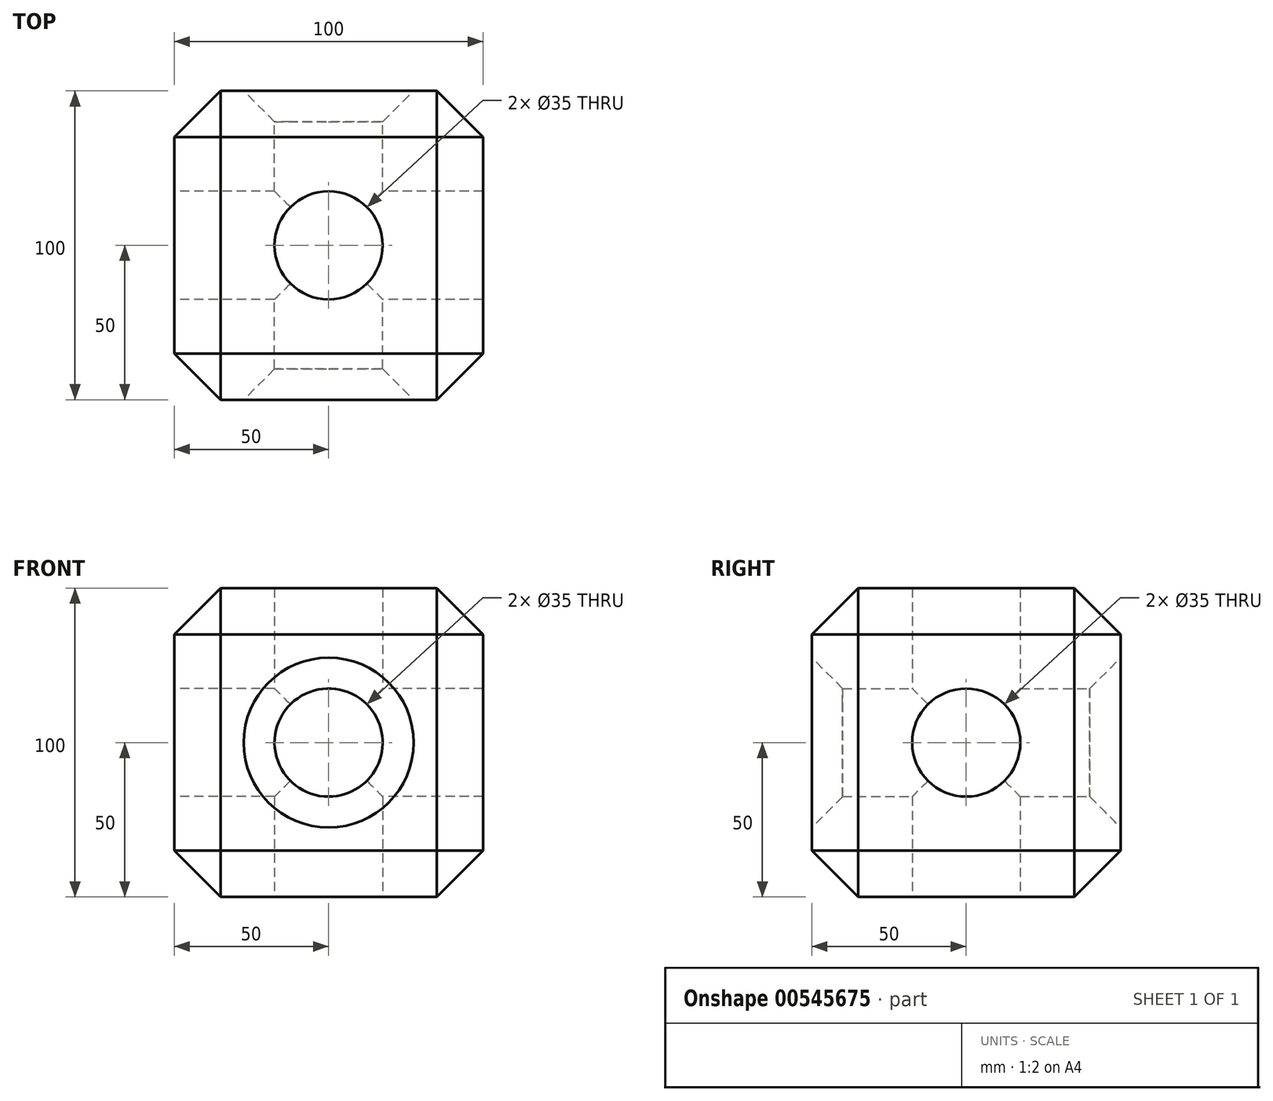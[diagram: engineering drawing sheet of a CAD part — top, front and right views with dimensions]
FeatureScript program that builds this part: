
annotation { "Feature Type Name" : "Feature", "Feature Type Description" : "" }
export const myFeature = defineFeature(function(context is Context, id is Id, definition is map)
    precondition{}
    {
        {
            var Q0;
            Q0=qCreatedBy(makeId("Front.planeOp"),FACE);
            var sketch = newSketch(context, id + "F0", { "sketchPlane" : qUnion([Q0])});
            skLineSegment(sketch, "E0.bottom", {"start": v(50, -50) * mm, "end": v(-50, -50) * mm});
            skLineSegment(sketch, "E0.top", {"start": v(50, 50) * mm, "end": v(-50, 50) * mm});
            skLineSegment(sketch, "E0.left", {"start": v(50, -50) * mm, "end": v(50, 50) * mm});
            skLineSegment(sketch, "E0.right", {"start": v(-50, -50) * mm, "end": v(-50, 50) * mm});
            skPoint(sketch, "E0.middle", {"position": v(0, 0) * mm});
            skCircle(sketch, "E1", {"center": v(0, 0) * mm, "radius": 17.5 * mm});
            skSolve(sketch);
        }
        {
            var Q0;
            Q0=makeQuery(id+"F0.imprint","IMPRINT",FACE,{"disambiguationData":[TD([[makeQuery(id+"F0.imprint","IMPRINT",EDGE,{"derivedFrom":sQuery(id+"F0.wireOp",EDGE,"E0.bottom")}),-1.0]])]});
            extrude(context, id + "F1", {"entities" : qUnion([Q0]), "endBound" : BoundingType.SYMMETRIC, "depth" : 100 * mm, "offsetDistance" : 25 * mm});
        }
        {
            var Q0;
            Q0=makeQuery(id+"F1.opExtrude","SWEPT_FACE",FACE,{"disambiguationData":[OSD([sQuery(id+"F0.wireOp",EDGE,"E0.right")])]});
            var sketch = newSketch(context, id + "F2", { "sketchPlane" : qUnion([Q0])});
            skCircle(sketch, "E2", {"center": v(0, 0) * mm, "radius": 17.5 * mm});
            skSolve(sketch);
        }
        {
            var Q0;
            Q0=makeQuery(id+"F2.imprint","IMPRINT",FACE,{"disambiguationData":[TD([[makeQuery(id+"F2.imprint","IMPRINT",EDGE,{"derivedFrom":sQuery(id+"F2.wireOp",EDGE,"E2")}),1.0]])]});
            var Q1;
            Q1=makeQuery(id+"F1.opExtrude","SWEPT_FACE",FACE,{"disambiguationData":[OSD([sQuery(id+"F0.wireOp",EDGE,"E0.left")])]});
            extrude(context, id + "F3", {"entities" : qUnion([Q0]), "operationType" : NewBodyOperationType.REMOVE, "endBound" : BoundingType.UP_TO_SURFACE, "oppositeDirection" : true, "depth" : 25 * mm, "endBoundEntityFace" : qUnion([Q1]), "offsetDistance" : 25 * mm});
        }
        {
            var Q0;
            Q0=makeQuery(id+"F1.opExtrude","SWEPT_FACE",FACE,{"disambiguationData":[OSD([sQuery(id+"F0.wireOp",EDGE,"E0.bottom")])]});
            var sketch = newSketch(context, id + "F4", { "sketchPlane" : qUnion([Q0])});
            skCircle(sketch, "E3", {"center": v(0, 0) * mm, "radius": 17.5 * mm});
            skSolve(sketch);
        }
        {
            var Q0;
            Q0=makeQuery(id+"F4.imprint","IMPRINT",FACE,{"disambiguationData":[TD([[makeQuery(id+"F4.imprint","IMPRINT",EDGE,{"derivedFrom":sQuery(id+"F4.wireOp",EDGE,"E3")}),1.0]])]});
            var Q1;
            Q1=makeQuery(id+"F1.opExtrude","SWEPT_FACE",FACE,{"disambiguationData":[OSD([sQuery(id+"F0.wireOp",EDGE,"E0.top")])]});
            extrude(context, id + "F5", {"entities" : qUnion([Q0]), "operationType" : NewBodyOperationType.REMOVE, "endBound" : BoundingType.UP_TO_SURFACE, "oppositeDirection" : true, "depth" : 25 * mm, "endBoundEntityFace" : qUnion([Q1]), "offsetDistance" : 25 * mm});
        }
        {
            var Q0;
            Q0=makeQuery(id+"F1.opExtrude","CAP_EDGE",EDGE,{"disambiguationData":[OSD([sQuery(id+"F0.wireOp",EDGE,"E0.top")])],"isStart":true});
            var Q1;
            Q1=makeQuery(id+"F1.opExtrude","SWEPT_EDGE",EDGE,{"disambiguationData":[OSD([sQuery(id+"F0.wireOp",EDGE,"E0.top"),sQuery(id+"F0.wireOp",EDGE,"E0.left")])]});
            var Q2;
            Q2=makeQuery(id+"F1.opExtrude","CAP_EDGE",EDGE,{"disambiguationData":[OSD([sQuery(id+"F0.wireOp",EDGE,"E0.top")])],"isStart":false});
            var Q3;
            Q3=makeQuery(id+"F1.opExtrude","SWEPT_EDGE",EDGE,{"disambiguationData":[OSD([sQuery(id+"F0.wireOp",EDGE,"E0.top"),sQuery(id+"F0.wireOp",EDGE,"E0.right")])]});
            var Q4;
            Q4=makeQuery(id+"F1.opExtrude","CAP_EDGE",EDGE,{"disambiguationData":[OSD([sQuery(id+"F0.wireOp",EDGE,"E0.right")])],"isStart":true});
            var Q5;
            Q5=makeQuery(id+"F1.opExtrude","CAP_EDGE",EDGE,{"disambiguationData":[OSD([sQuery(id+"F0.wireOp",EDGE,"E0.right")])],"isStart":false});
            var Q6;
            Q6=makeQuery(id+"F1.opExtrude","SWEPT_EDGE",EDGE,{"disambiguationData":[OSD([sQuery(id+"F0.wireOp",EDGE,"E0.bottom"),sQuery(id+"F0.wireOp",EDGE,"E0.right")])]});
            var Q7;
            Q7=makeQuery(id+"F1.opExtrude","CAP_EDGE",EDGE,{"disambiguationData":[OSD([sQuery(id+"F0.wireOp",EDGE,"E0.bottom")])],"isStart":true});
            var Q8;
            Q8=makeQuery(id+"F1.opExtrude","SWEPT_EDGE",EDGE,{"disambiguationData":[OSD([sQuery(id+"F0.wireOp",EDGE,"E0.bottom"),sQuery(id+"F0.wireOp",EDGE,"E0.left")])]});
            var Q9;
            Q9=makeQuery(id+"F1.opExtrude","CAP_EDGE",EDGE,{"disambiguationData":[OSD([sQuery(id+"F0.wireOp",EDGE,"E0.left")])],"isStart":false});
            var Q10;
            Q10=makeQuery(id+"F1.opExtrude","CAP_EDGE",EDGE,{"disambiguationData":[OSD([sQuery(id+"F0.wireOp",EDGE,"E0.bottom")])],"isStart":false});
            var Q11;
            Q11=makeQuery(id+"F1.opExtrude","CAP_EDGE",EDGE,{"disambiguationData":[OSD([sQuery(id+"F0.wireOp",EDGE,"E0.left")])],"isStart":true});
            chamfer(context, id + "F6", {"entities" : qUnion([Q0, Q1, Q2, Q3, Q4, Q5, Q6, Q7, Q8, Q9, Q10, Q11]), "width" : 15 * mm, "tangentPropagation" : true});
        }
        {
            var Q0;
            Q0=makeQuery(id+"F3.boolean.opBoolean","COPY",EDGE,{"derivedFrom":makeQuery(id+"F3.opExtrude","TWEAK_EDGE",EDGE,{"derivedFrom":[makeQuery(id+"F1.opExtrude","SWEPT_FACE",FACE,{"disambiguationData":[OSD([sQuery(id+"F0.wireOp",EDGE,"E0.left")])]}),makeQuery(id+"F2.imprint","IMPRINT",EDGE,{"derivedFrom":sQuery(id+"F2.wireOp",EDGE,"E2")})]})});
            var Q1;
            Q1=makeQuery(id+"F1.opExtrude","CAP_EDGE",EDGE,{"disambiguationData":[OSD([sQuery(id+"F0.wireOp",EDGE,"E1")])],"isStart":true});
            var Q2;
            Q2=makeQuery(id+"F5.boolean.opBoolean","COPY",EDGE,{"derivedFrom":makeQuery(id+"F5.opExtrude","CAP_EDGE",EDGE,{"disambiguationData":[OSD([sQuery(id+"F4.wireOp",EDGE,"E3")])],"isStart":true})});
            var Q3;
            Q3=makeQuery(id+"F1.opExtrude","CAP_EDGE",EDGE,{"disambiguationData":[OSD([sQuery(id+"F0.wireOp",EDGE,"E1")])],"isStart":false});
            var Q4;
            Q4=makeQuery(id+"F3.boolean.opBoolean","COPY",EDGE,{"derivedFrom":makeQuery(id+"F3.opExtrude","CAP_EDGE",EDGE,{"disambiguationData":[OSD([sQuery(id+"F2.wireOp",EDGE,"E2")])],"isStart":true})});
            var Q5;
            Q5=makeQuery(id+"F5.boolean.opBoolean","COPY",EDGE,{"derivedFrom":makeQuery(id+"F5.opExtrude","TWEAK_EDGE",EDGE,{"derivedFrom":[makeQuery(id+"F1.opExtrude","SWEPT_FACE",FACE,{"disambiguationData":[OSD([sQuery(id+"F0.wireOp",EDGE,"E0.top")])]}),makeQuery(id+"F4.imprint","IMPRINT",EDGE,{"derivedFrom":sQuery(id+"F4.wireOp",EDGE,"E3")})]})});
            chamfer(context, id + "F7", {"entities" : qUnion([Q0, Q1, Q2, Q3, Q4, Q5]), "width" : 10 * mm, "tangentPropagation" : true});
        }
    });
